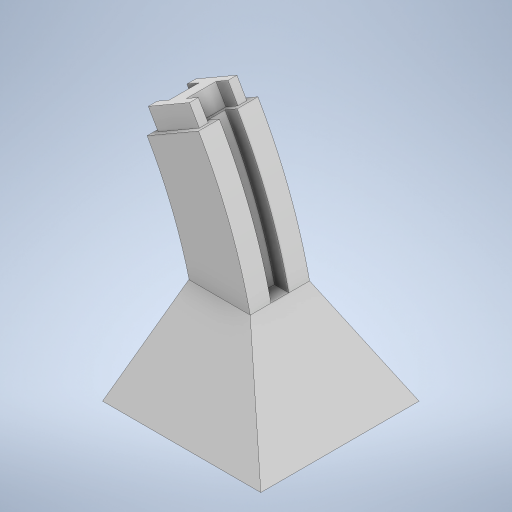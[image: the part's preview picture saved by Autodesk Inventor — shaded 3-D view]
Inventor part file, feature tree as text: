
AUTODESK INVENTOR PART (.ipt)
format: ipt  version: 2023 (Build 270158000, 158)  size: 404,992 bytes
history: native  units: mm
features: sketch x11, extrude x5, plane x4, loft x2, sweep x1
ambient origin geometry x8: Origin, YZ Plane, XZ Plane, XY Plane, X Axis, Y Axis, Z Axis, Center Point
bodies: Body1 (feature_tree)
feature tree (23):
  sweep  "Sweep2"
  extrude  "Extrusion3"  Depth=7.0mm
  extrude  "Extrusion4"  Depth=15.0mm
  sketch  "Sketch9"  dims[d41=220.0mm d42=60.0deg]
  plane  "Work Plane1"
  loft  "Loft1"
  plane  "Work Plane2"
  extrude  "Extrusion5"  TaperAngle=60.0deg  [1 undecoded]
  sketch  "Sketch12"  dims[d48=3.0mm d49=3.0mm]
  plane  "Work Plane3"
  loft  "Loft2"
  plane  "Work Plane4"
  extrude  "Extrusion6"  Depth=3.0mm
  extrude  "Extrusion7"  Depth=3.0mm
  sketch  "Sketch2"  dims[d5=100.0mm d18=9.0mm]
  sketch  "Sketch6"  dims[d19=7.0mm d21=16.0mm]
  sketch  "Sketch7"  dims[d22=30.0mm d23=15.0mm]
  sketch  "Sketch8"  dims[d24=4.5mm d25=8.0mm]
  sketch  "Sketch10"  dims[d43=220.0mm d44=0.0mm]
  sketch  "Sketch11"  dims[d45=0.0mm d46=0.0mm d47=3.0mm]
  sketch  "Sketch14"  dims[d50=3.0mm]
  sketch  "Sketch15"  dims[d51=3.0mm]
  sketch  "Sketch16"  dims[d52=3.0mm d53=3.0mm d54=3.0mm d55=3.0mm d56=10.0mm d57=0.0mm d58=4.0mm d59=12.0mm d60=5.0mm d61=0.0mm d62=0.0mm d63=80.0mm d64=80.0mm d65=40.0mm d66=40.0mm d67=50.0mm d68=30.0mm d69=9.6mm d70=15.0mm d71=31.0mm d72=0.0mm d73=90.0deg d74=0.0mm d75=90.0deg d76=-79.0mm d77=100.0mm d79=140.0mm d80=67.608902mm d81=140.0mm d82=150.0deg d83=50.0mm d84=0.0mm d85=0.0mm d86=5.0mm d87=10.0mm d88=10.0mm d89=10.0mm d90=10.0mm d91=-45.0mm d95=1.0mm d96=1.0mm d97=39.5mm d98=39.5mm d99=0.0mm d100=90.0deg d101=0.0mm d102=90.0deg d103=30.0mm d105=220.0mm d107=0.0mm d108=30.0deg d109=220.0mm d110=0.0mm d111=0.0mm d112=3.0mm d113=3.0mm d114=3.0mm d115=3.0mm d116=3.0mm d117=3.0mm d118=3.0mm d119=3.0mm d120=3.0mm d121=10.0mm d122=0.0mm]
note: 1 required parameter value undecoded (feature->parameter linkage not recoverable at this tier; creation-order binding heuristic only, values carry confidence <= 0.55)
